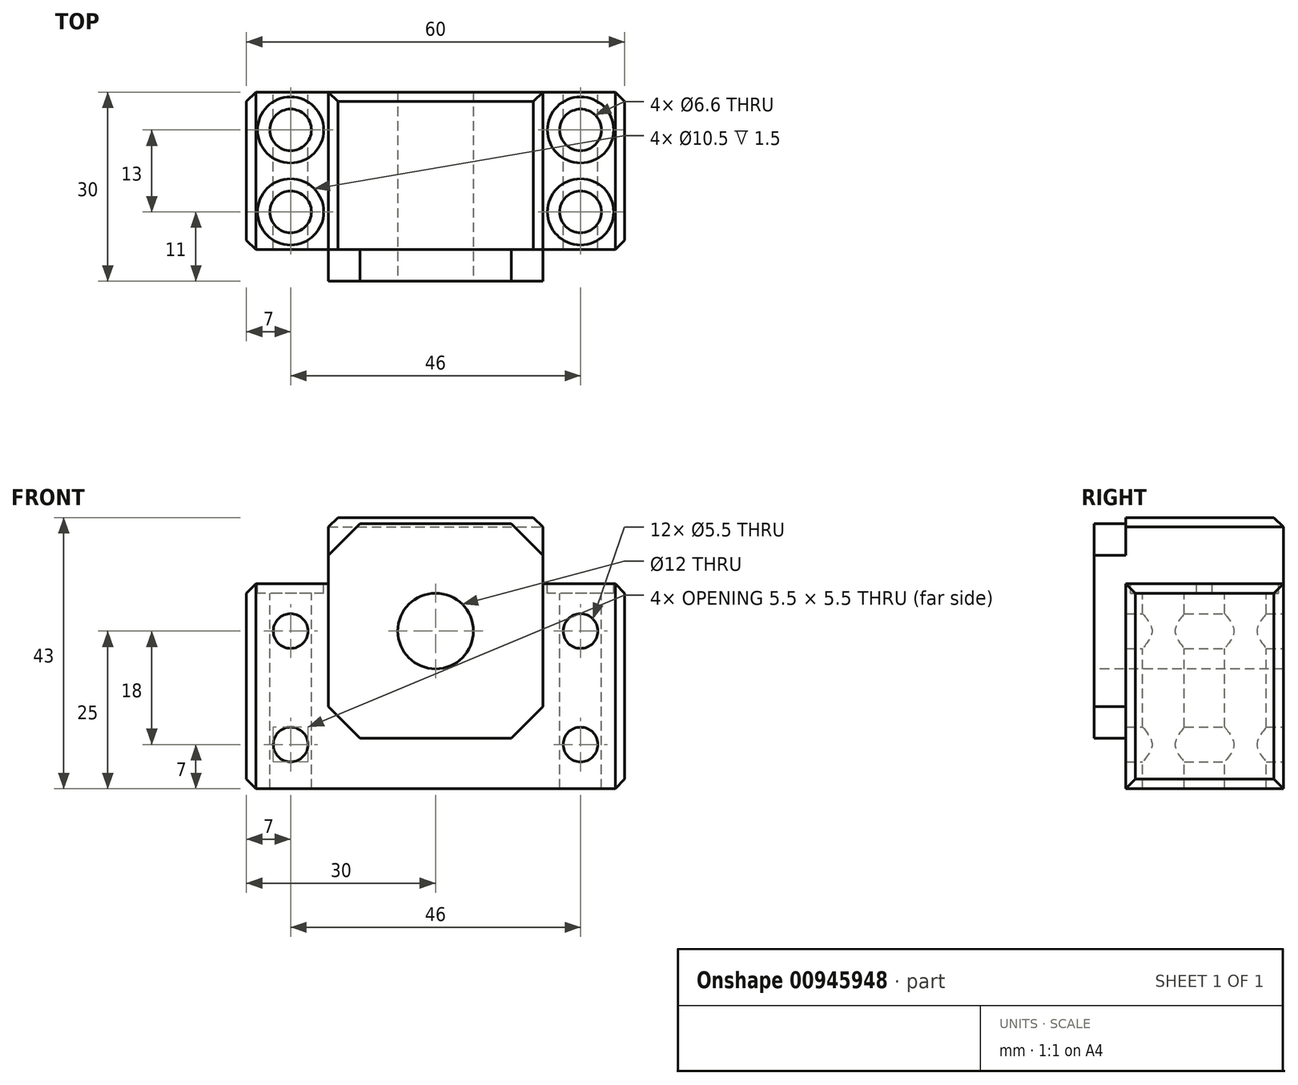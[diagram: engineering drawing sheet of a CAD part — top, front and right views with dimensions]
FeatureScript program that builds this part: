
annotation { "Feature Type Name" : "Feature", "Feature Type Description" : "" }
export const myFeature = defineFeature(function(context is Context, id is Id, definition is map)
    precondition{}
    {
        {
            var Q0;
            Q0=qCreatedBy(makeId("Front.planeOp"),FACE);
            var sketch = newSketch(context, id + "F0", { "sketchPlane" : qUnion([Q0])});
            skLineSegment(sketch, "E0.bottom", {"start": v(30, -25) * mm, "end": v(-30, -25) * mm});
            skLineSegment(sketch, "E0.top", {"start": v(30, 7.5) * mm, "end": v(17, 7.5) * mm});
            skLineSegment(sketch, "E0.left", {"start": v(30, -25) * mm, "end": v(30, 7.5) * mm});
            skLineSegment(sketch, "E0.right", {"start": v(-30, -25) * mm, "end": v(-30, 7.5) * mm});
            skPoint(sketch, "E0.middle", {"position": v(0, -8.75) * mm});
            skLineSegment(sketch, "E1.top", {"start": v(17, 18) * mm, "end": v(-17, 18) * mm});
            skLineSegment(sketch, "E1.left", {"start": v(17, 7.5) * mm, "end": v(17, 18) * mm});
            skLineSegment(sketch, "E1.right", {"start": v(-17, 7.5) * mm, "end": v(-17, 18) * mm});
            skPoint(sketch, "E1.middle", {"position": v(0, 12.75) * mm});
            skLineSegment(sketch, "E2.trimOffspring", {"start": v(-17, 7.5) * mm, "end": v(-30, 7.5) * mm});
            skCircle(sketch, "E3", {"center": v(0, 0) * mm, "radius": 13 * mm});
            skCircle(sketch, "E4", {"center": v(-23, 0) * mm, "radius": 2.75 * mm});
            skCircle(sketch, "E5", {"center": v(-23, -18) * mm, "radius": 2.75 * mm});
            skLineSegment(sketch, "E6", {"start": v(0, 18) * mm, "end": v(0, -25) * mm, "construction": true});
            skCircle(sketch, "E7.MirrorC", {"center": v(23, -18) * mm, "radius": 2.75 * mm});
            skCircle(sketch, "E8.MirrorC", {"center": v(23, 0) * mm, "radius": 2.75 * mm});
            skSolve(sketch);
        }
        {
            var Q0;
            Q0 = qSketchRegion(id + "F0", true);
            extrude(context, id + "F1", {"entities" : qUnion([Q0]), "depth" : 25 * mm, "offsetDistance" : 25 * mm});
        }
        {
            var Q0;
            Q0=makeQuery(id+"F1.opExtrude","CAP_FACE",FACE,{"disambiguationData":[OSD([sQuery(id+"F0.wireOp",EDGE,"E0.bottom"),sQuery(id+"F0.wireOp",EDGE,"E0.top"),sQuery(id+"F0.wireOp",EDGE,"E0.left"),sQuery(id+"F0.wireOp",EDGE,"E0.right"),sQuery(id+"F0.wireOp",EDGE,"E1.top"),sQuery(id+"F0.wireOp",EDGE,"E1.left"),sQuery(id+"F0.wireOp",EDGE,"E1.right"),sQuery(id+"F0.wireOp",EDGE,"E2.trimOffspring"),sQuery(id+"F0.wireOp",EDGE,"E3"),sQuery(id+"F0.wireOp",EDGE,"E4"),sQuery(id+"F0.wireOp",EDGE,"E5"),sQuery(id+"F0.wireOp",EDGE,"E7.MirrorC"),sQuery(id+"F0.wireOp",EDGE,"E8.MirrorC")])],"isStart":false});
            var sketch = newSketch(context, id + "F2", { "sketchPlane" : qUnion([Q0])});
            skLineSegment(sketch, "E9.bottom", {"start": v(17, -17) * mm, "end": v(-17, -17) * mm});
            skLineSegment(sketch, "E9.top", {"start": v(17, 17) * mm, "end": v(-17, 17) * mm});
            skLineSegment(sketch, "E9.left", {"start": v(17, -17) * mm, "end": v(17, 17) * mm});
            skLineSegment(sketch, "E9.right", {"start": v(-17, -17) * mm, "end": v(-17, 17) * mm});
            skPoint(sketch, "E9.middle", {"position": v(0, 0) * mm});
            skCircle(sketch, "E10.0", {"center": v(0, 0) * mm, "radius": 13 * mm});
            skSolve(sketch);
        }
        {
            var Q0;
            Q0 = qSketchRegion(id + "F2", true);
            extrude(context, id + "F3", {"entities" : qUnion([Q0]), "operationType" : NewBodyOperationType.ADD, "depth" : 5 * mm, "offsetDistance" : 25 * mm});
        }
        {
            var Q0;
            Q0=makeQuery(id+"F3.opExtrude","SWEPT_EDGE",EDGE,{"disambiguationData":[OSD([sQuery(id+"F0.wireOp",EDGE,"E1.right"),sQuery(id+"F2.wireOp",EDGE,"E9.top"),sQuery(id+"F2.wireOp",EDGE,"E9.right")])]});
            var Q1;
            Q1=makeQuery(id+"F3.opExtrude","SWEPT_EDGE",EDGE,{"disambiguationData":[OSD([sQuery(id+"F0.wireOp",EDGE,"E1.left"),sQuery(id+"F2.wireOp",EDGE,"E9.top"),sQuery(id+"F2.wireOp",EDGE,"E9.left")])]});
            var Q2;
            Q2=makeQuery(id+"F3.opExtrude","SWEPT_EDGE",EDGE,{"disambiguationData":[OSD([sQuery(id+"F2.wireOp",EDGE,"E9.bottom"),sQuery(id+"F2.wireOp",EDGE,"E9.left")])]});
            var Q3;
            Q3=makeQuery(id+"F3.opExtrude","SWEPT_EDGE",EDGE,{"disambiguationData":[OSD([sQuery(id+"F2.wireOp",EDGE,"E9.bottom"),sQuery(id+"F2.wireOp",EDGE,"E9.right")])]});
            chamfer(context, id + "F4", {"entities" : qUnion([Q0, Q1, Q2, Q3]), "width" : 5 * mm, "tangentPropagation" : true});
        }
        {
            var Q0;
            Q0=makeQuery(id+"F1.opExtrude","SWEPT_EDGE",EDGE,{"disambiguationData":[OSD([sQuery(id+"F0.wireOp",EDGE,"E1.top"),sQuery(id+"F0.wireOp",EDGE,"E1.right")])]});
            var Q1;
            Q1=makeQuery(id+"F1.opExtrude","SWEPT_EDGE",EDGE,{"disambiguationData":[OSD([sQuery(id+"F0.wireOp",EDGE,"E1.top"),sQuery(id+"F0.wireOp",EDGE,"E1.left")])]});
            var Q2;
            Q2=makeQuery(id+"F1.opExtrude","CAP_EDGE",EDGE,{"disambiguationData":[OSD([sQuery(id+"F0.wireOp",EDGE,"E1.top")])],"isStart":true});
            var Q3;
            Q3=makeQuery(id+"F1.opExtrude","SWEPT_EDGE",EDGE,{"disambiguationData":[OSD([sQuery(id+"F0.wireOp",EDGE,"E0.right"),sQuery(id+"F0.wireOp",EDGE,"E2.trimOffspring")])]});
            var Q4;
            Q4=makeQuery(id+"F1.opExtrude","CAP_EDGE",EDGE,{"disambiguationData":[OSD([sQuery(id+"F0.wireOp",EDGE,"E0.right")])],"isStart":false});
            var Q5;
            Q5=makeQuery(id+"F1.opExtrude","CAP_EDGE",EDGE,{"disambiguationData":[OSD([sQuery(id+"F0.wireOp",EDGE,"E0.right")])],"isStart":true});
            var Q6;
            Q6=makeQuery(id+"F1.opExtrude","SWEPT_EDGE",EDGE,{"disambiguationData":[OSD([sQuery(id+"F0.wireOp",EDGE,"E0.bottom"),sQuery(id+"F0.wireOp",EDGE,"E0.right")])]});
            var Q7;
            Q7=makeQuery(id+"F1.opExtrude","CAP_EDGE",EDGE,{"disambiguationData":[OSD([sQuery(id+"F0.wireOp",EDGE,"E0.left")])],"isStart":false});
            var Q8;
            Q8=makeQuery(id+"F1.opExtrude","SWEPT_EDGE",EDGE,{"disambiguationData":[OSD([sQuery(id+"F0.wireOp",EDGE,"E0.top"),sQuery(id+"F0.wireOp",EDGE,"E0.left")])]});
            var Q9;
            Q9=makeQuery(id+"F1.opExtrude","CAP_EDGE",EDGE,{"disambiguationData":[OSD([sQuery(id+"F0.wireOp",EDGE,"E0.left")])],"isStart":true});
            var Q10;
            Q10=makeQuery(id+"F1.opExtrude","SWEPT_EDGE",EDGE,{"disambiguationData":[OSD([sQuery(id+"F0.wireOp",EDGE,"E0.bottom"),sQuery(id+"F0.wireOp",EDGE,"E0.left")])]});
            chamfer(context, id + "F5", {"entities" : qUnion([Q0, Q1, Q2, Q3, Q4, Q5, Q6, Q7, Q8, Q9, Q10]), "width" : 1.5 * mm, "tangentPropagation" : true});
        }
        {
            var Q0;
            Q0=makeQuery(id+"F1.opExtrude","SWEPT_FACE",FACE,{"disambiguationData":[OSD([sQuery(id+"F0.wireOp",EDGE,"E0.top")])]});
            var sketch = newSketch(context, id + "F6", { "sketchPlane" : qUnion([Q0])});
            skCircle(sketch, "E11", {"center": v(23, -6) * mm, "radius": 3.3 * mm});
            skCircle(sketch, "E12", {"center": v(23, -19) * mm, "radius": 3.3 * mm});
            skLineSegment(sketch, "E13", {"start": v(0, 0) * mm, "end": v(0, -50.16) * mm, "construction": true});
            skCircle(sketch, "E14.MirrorC", {"center": v(-23, -19) * mm, "radius": 3.3 * mm});
            skCircle(sketch, "E15.MirrorC", {"center": v(-23, -6) * mm, "radius": 3.3 * mm});
            skSolve(sketch);
        }
        {
            var Q0;
            Q0 = qSketchRegion(id + "F6", true);
            extrude(context, id + "F7", {"entities" : qUnion([Q0]), "operationType" : NewBodyOperationType.REMOVE, "endBound" : BoundingType.THROUGH_ALL, "oppositeDirection" : true, "depth" : 25 * mm, "offsetDistance" : 25 * mm});
        }
        {
            var Q0;
            Q0=makeQuery(id+"F3.opExtrude","CAP_FACE",FACE,{"disambiguationData":[OSD([sQuery(id+"F2.wireOp",EDGE,"E9.bottom"),sQuery(id+"F2.wireOp",EDGE,"E9.top"),sQuery(id+"F2.wireOp",EDGE,"E9.left"),sQuery(id+"F2.wireOp",EDGE,"E9.right"),sQuery(id+"F2.wireOp",EDGE,"E10.0")])],"isStart":false});
            var sketch = newSketch(context, id + "F8", { "sketchPlane" : qUnion([Q0])});
            skCircle(sketch, "E16", {"center": v(0, 0) * mm, "radius": 13 * mm});
            skCircle(sketch, "E17", {"center": v(0, 0) * mm, "radius": 6 * mm});
            skSolve(sketch);
        }
        {
            var Q0;
            Q0=makeQuery(id+"F8.imprint","IMPRINT",FACE,{"disambiguationData":[TD([[makeQuery(id+"F8.imprint","IMPRINT",EDGE,{"derivedFrom":sQuery(id+"F8.wireOp",EDGE,"E16")}),1.0]])]});
            var Q1;
            Q1=makeQuery(id+"F1.opExtrude","CAP_FACE",FACE,{"disambiguationData":[OSD([sQuery(id+"F0.wireOp",EDGE,"E0.bottom"),sQuery(id+"F0.wireOp",EDGE,"E0.top"),sQuery(id+"F0.wireOp",EDGE,"E0.left"),sQuery(id+"F0.wireOp",EDGE,"E0.right"),sQuery(id+"F0.wireOp",EDGE,"E1.top"),sQuery(id+"F0.wireOp",EDGE,"E1.left"),sQuery(id+"F0.wireOp",EDGE,"E1.right"),sQuery(id+"F0.wireOp",EDGE,"E2.trimOffspring"),sQuery(id+"F0.wireOp",EDGE,"E3"),sQuery(id+"F0.wireOp",EDGE,"E4"),sQuery(id+"F0.wireOp",EDGE,"E5"),sQuery(id+"F0.wireOp",EDGE,"E7.MirrorC"),sQuery(id+"F0.wireOp",EDGE,"E8.MirrorC")])],"isStart":true});
            extrude(context, id + "F9", {"entities" : qUnion([Q0]), "operationType" : NewBodyOperationType.ADD, "endBound" : BoundingType.UP_TO_SURFACE, "oppositeDirection" : true, "depth" : 25 * mm, "endBoundEntityFace" : qUnion([Q1]), "offsetDistance" : 25 * mm});
        }
        {
            var Q0;
            Q0=makeQuery(id+"F1.opExtrude","SWEPT_FACE",FACE,{"disambiguationData":[OSD([sQuery(id+"F0.wireOp",EDGE,"E2.trimOffspring")])]});
            var sketch = newSketch(context, id + "F10", { "sketchPlane" : qUnion([Q0])});
            skCircle(sketch, "E18", {"center": v(-23, -6) * mm, "radius": 5.25 * mm});
            skCircle(sketch, "E19", {"center": v(-23, -19) * mm, "radius": 5.25 * mm});
            skLineSegment(sketch, "E20", {"start": v(0, 1.72) * mm, "end": v(0, -34.94) * mm, "construction": true});
            skCircle(sketch, "E21.MirrorC", {"center": v(23, -6) * mm, "radius": 5.25 * mm});
            skCircle(sketch, "E22.MirrorC", {"center": v(23, -19) * mm, "radius": 5.25 * mm});
            skSolve(sketch);
        }
        {
            var Q0;
            Q0 = qSketchRegion(id + "F10", true);
            extrude(context, id + "F11", {"entities" : qUnion([Q0]), "operationType" : NewBodyOperationType.REMOVE, "oppositeDirection" : true, "depth" : 1.5 * mm, "offsetDistance" : 25 * mm});
        }
    });
